FCSTD DOCUMENT  (FreeCAD 1.0R39109 (Git))
Label: lock_tube
License: All rights reserved
LicenseURL: https://en.wikipedia.org/wiki/All_rights_reserved
objects: Sketcher::SketchObject×1
note: 2 computed .brp shape members not serialized (recipe doc carries the construction recipe); baked Part::Feature solids carry a one-line shape summary decoded from their .brp

FEATURE [Sketcher::SketchObject] Sketch
  ArcFitTolerance = 1e-06
  FullyConstrained = true
  MakeInternals = false
  sketch-geometry (6):
    g0: ArcOfCircle CenterX=0 CenterY=0 CenterZ=0 NormalX=0 NormalY=0 NormalZ=1 AngleXU=0 Radius=65 StartAngle=0.617403 EndAngle=5.66578
    g1: LineSegment StartX=53 StartY=37.6298 StartZ=0 EndX=68 EndY=7.5 EndZ=0
    g2: LineSegment StartX=68 StartY=-7.5 StartZ=0 EndX=53 EndY=-37.6298 EndZ=0
    g3: Circle CenterX=0 CenterY=0 CenterZ=0 NormalX=0 NormalY=0 NormalZ=1 AngleXU=0 Radius=57
    g4: ArcOfCircle CenterX=68 CenterY=0 CenterZ=0 NormalX=0 NormalY=0 NormalZ=1 AngleXU=0 Radius=7.5 StartAngle=4.71239 EndAngle=7.85398
    g5: Circle CenterX=68 CenterY=0 CenterZ=0 NormalX=0 NormalY=0 NormalZ=1 AngleXU=0 Radius=4
  constraints (17):
    c: Coincident(g0,g-1)
    c: Diameter(g0) = 130
    c: Coincident(g3,g0)
    c: Diameter(g3) = 114
    c: Diameter(g4) = 15
    c: Coincident(g5,g4)
    c: Diameter(g5) = 8
    c: Coincident(g4,g1)
    c: Coincident(g4,g2)
    c: DistanceX(g2,g1) = 0
    c: Coincident(g0,g1)
    c: Coincident(g2,g0)
    c: DistanceX(g0,g4) = 15
    c: DistanceY(g4,g0) = 0
    c: DistanceX(g0,g4) = 68
    c: DistanceX(g1,g4) = 0
    c: DistanceX(g0,g2) = 15
